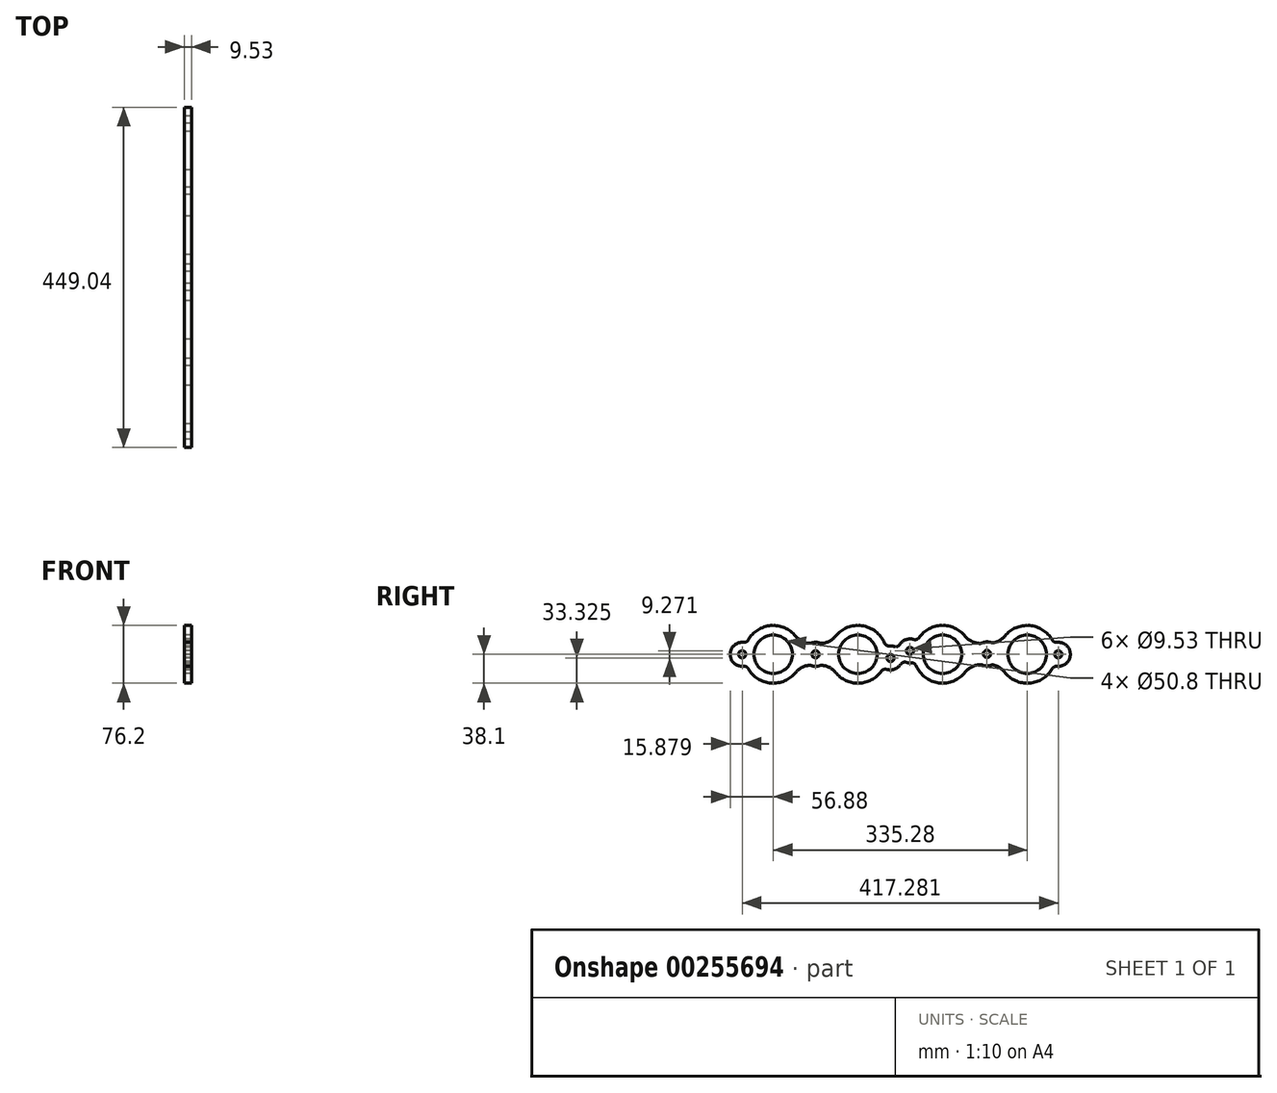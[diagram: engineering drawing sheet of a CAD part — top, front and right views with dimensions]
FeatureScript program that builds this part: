
annotation { "Feature Type Name" : "Feature", "Feature Type Description" : "" }
export const myFeature = defineFeature(function(context is Context, id is Id, definition is map)
    precondition{}
    {
        {
            var Q0;
            Q0=qCreatedBy(makeId("Right.planeOp"),FACE);
            cPlane(context, id + "F0", {"entities" : qUnion([Q0]), "cplaneType" : CPlaneType.OFFSET, "offset" : 203.2 * mm, "oppositeDirection" : true, "width" : 152.4 * mm, "height" : 152.4 * mm});
        }
        {
            var Q0;
            Q0=qCreatedBy(makeId("Top.planeOp"),FACE);
            cPlane(context, id + "F1", {"entities" : qUnion([Q0]), "cplaneType" : CPlaneType.OFFSET, "offset" : 111.76 * mm, "width" : 152.4 * mm, "height" : 152.4 * mm});
        }
        {
            var Q0;
            Q0=qCreatedBy(makeId("Front.planeOp"),FACE);
            var sketch = newSketch(context, id + "F2", { "sketchPlane" : qUnion([Q0])});
            skCircle(sketch, "E0", {"center": v(0, 0) * mm, "radius": 44.45 * mm});
            skCircle(sketch, "E1", {"center": v(0, 0) * mm, "radius": 38.1 * mm});
            skCircle(sketch, "E2", {"center": v(0, 0) * mm, "radius": 57.15 * mm});
            skSolve(sketch);
        }
        {
            var Q0;
            Q0=qCreatedBy(id+"F0.planeOp",FACE);
            var sketch = newSketch(context, id + "F3", { "sketchPlane" : qUnion([Q0])});
            skCircle(sketch, "E3", {"center": v(129.54, 111.76) * mm, "radius": 31.75 * mm});
            skCircle(sketch, "E4.1.0.0", {"center": v(241.3, 111.76) * mm, "radius": 31.75 * mm});
            skCircle(sketch, "E4.2.0.0", {"center": v(353.06, 111.76) * mm, "radius": 31.75 * mm});
            skCircle(sketch, "E4.3.0.0", {"center": v(464.82, 111.76) * mm, "radius": 31.75 * mm});
            skLineSegment(sketch, "E4.direction1", {"start": v(129.54, 111.76) * mm, "end": v(241.3, 111.76) * mm, "construction": true});
            skCircle(sketch, "E5", {"center": v(464.82, 111.76) * mm, "radius": 25.4 * mm});
            skCircle(sketch, "E6", {"center": v(353.06, 111.76) * mm, "radius": 25.4 * mm});
            skCircle(sketch, "E7", {"center": v(241.3, 111.76) * mm, "radius": 25.4 * mm});
            skCircle(sketch, "E8", {"center": v(129.54, 111.76) * mm, "radius": 25.4 * mm});
            skArc(sketch, "E9", {"start": v(497.88, 130.7) * mm, "mid": v(467.97, 149.73) * mm, "end": v(435.33, 135.88) * mm});
            skArc(sketch, "E10", {"start": v(191.04, 126.6) * mm, "mid": v(185.42, 127.64) * mm, "end": v(179.8, 126.6) * mm});
            skCircle(sketch, "E11", {"center": v(185.42, 111.76) * mm, "radius": 4.76 * mm});
            skCircle(sketch, "E12", {"center": v(88.54, 111.76) * mm, "radius": 4.76 * mm});
            skArc(sketch, "E13", {"start": v(90.27, 127.54) * mm, "mid": v(72.66, 111.76) * mm, "end": v(90.27, 95.98) * mm});
            skCircle(sketch, "E14", {"center": v(411.61, 112.33) * mm, "radius": 4.76 * mm});
            skCircle(sketch, "E15", {"center": v(505.82, 111.76) * mm, "radius": 4.76 * mm});
            skCircle(sketch, "E16", {"center": v(310.06, 116.26) * mm, "radius": 4.76 * mm});
            skCircle(sketch, "E17", {"center": v(284.3, 106.98) * mm, "radius": 4.76 * mm});
            skArc(sketch, "E18.trimOffspring", {"start": v(504.09, 95.98) * mm, "mid": v(521.7, 111.76) * mm, "end": v(504.09, 127.54) * mm});
            skPoint(sketch, "E19.visualSharp", {"position": v(94.41, 126.5) * mm});
            skArc(sketch, "E19.filletArc", {"start": v(90.27, 127.54) * mm, "mid": v(93.85, 128.2) * mm, "end": v(96.48, 130.7) * mm});
            skPoint(sketch, "E20.visualSharp", {"position": v(94.41, 97.01) * mm});
            skArc(sketch, "E20.filletArc", {"start": v(96.48, 92.82) * mm, "mid": v(93.85, 95.33) * mm, "end": v(90.27, 95.98) * mm});
            skPoint(sketch, "E21.visualSharp", {"position": v(499.95, 126.5) * mm});
            skArc(sketch, "E21.filletArc", {"start": v(497.88, 130.7) * mm, "mid": v(500.51, 128.2) * mm, "end": v(504.09, 127.54) * mm});
            skPoint(sketch, "E22.visualSharp", {"position": v(499.95, 97.01) * mm});
            skArc(sketch, "E22.filletArc", {"start": v(504.09, 95.98) * mm, "mid": v(500.51, 95.33) * mm, "end": v(497.88, 92.82) * mm});
            skArc(sketch, "E23", {"start": v(276.38, 126.63) * mm, "mid": v(246.54, 149.5) * mm, "end": v(211.6, 135.63) * mm});
            skArc(sketch, "E24", {"start": v(318.08, 96.66) * mm, "mid": v(348.18, 73.97) * mm, "end": v(383.06, 88.27) * mm});
            skArc(sketch, "E25", {"start": v(305.1, 101.18) * mm, "mid": v(308.32, 100.48) * mm, "end": v(311.62, 100.46) * mm});
            skArc(sketch, "E26", {"start": v(289.26, 122.06) * mm, "mid": v(286.08, 122.76) * mm, "end": v(282.82, 122.8) * mm});
            skArc(sketch, "E27.trimOffspring", {"start": v(314.86, 131.39) * mm, "mid": v(304.6, 131.16) * mm, "end": v(296.62, 124.71) * mm});
            skArc(sketch, "E28.trimOffspring", {"start": v(279.39, 91.9) * mm, "mid": v(289.7, 92.06) * mm, "end": v(297.74, 98.53) * mm});
            skPoint(sketch, "E29.visualSharp", {"position": v(275.05, 94.08) * mm});
            skArc(sketch, "E29.filletArc", {"start": v(279.39, 91.9) * mm, "mid": v(275.44, 91.89) * mm, "end": v(272.26, 89.55) * mm});
            skPoint(sketch, "E30.visualSharp", {"position": v(278.1, 121.6) * mm});
            skArc(sketch, "E30.filletArc", {"start": v(276.38, 126.63) * mm, "mid": v(278.97, 123.66) * mm, "end": v(282.82, 122.8) * mm});
            skPoint(sketch, "E31.visualSharp", {"position": v(294.46, 119.19) * mm});
            skArc(sketch, "E31.filletArc", {"start": v(289.26, 122.06) * mm, "mid": v(293.4, 122.12) * mm, "end": v(296.62, 124.71) * mm});
            skPoint(sketch, "E32.visualSharp", {"position": v(319.2, 129.23) * mm});
            skArc(sketch, "E32.filletArc", {"start": v(314.86, 131.39) * mm, "mid": v(318.8, 131.42) * mm, "end": v(321.96, 133.77) * mm});
            skPoint(sketch, "E33.visualSharp", {"position": v(316.32, 101.67) * mm});
            skArc(sketch, "E33.filletArc", {"start": v(318.08, 96.66) * mm, "mid": v(315.47, 99.61) * mm, "end": v(311.62, 100.46) * mm});
            skPoint(sketch, "E34.visualSharp", {"position": v(299.9, 104.05) * mm});
            skArc(sketch, "E34.filletArc", {"start": v(305.1, 101.18) * mm, "mid": v(300.96, 101.12) * mm, "end": v(297.74, 98.53) * mm});
            skArc(sketch, "E35", {"start": v(96.48, 92.82) * mm, "mid": v(126.56, 73.78) * mm, "end": v(159.24, 87.9) * mm});
            skArc(sketch, "E36.trimOffspring", {"start": v(159.24, 135.63) * mm, "mid": v(126.56, 149.74) * mm, "end": v(96.48, 130.7) * mm});
            skArc(sketch, "E37.trimOffspring", {"start": v(211.6, 87.9) * mm, "mid": v(242.34, 73.67) * mm, "end": v(272.26, 89.55) * mm});
            skPoint(sketch, "E38.visualSharp", {"position": v(164.82, 126.14) * mm});
            skArc(sketch, "E38.filletArc", {"start": v(159.24, 135.63) * mm, "mid": v(167.17, 129.08) * mm, "end": v(177.05, 126.21) * mm});
            skPoint(sketch, "E39.visualSharp", {"position": v(164.82, 97.38) * mm});
            skArc(sketch, "E39.filletArc", {"start": v(177.05, 97.3) * mm, "mid": v(167.17, 94.44) * mm, "end": v(159.24, 87.9) * mm});
            skPoint(sketch, "E40.visualSharp", {"position": v(206.02, 126.14) * mm});
            skArc(sketch, "E40.filletArc", {"start": v(193.79, 126.21) * mm, "mid": v(203.67, 129.08) * mm, "end": v(211.6, 135.63) * mm});
            skPoint(sketch, "E41.visualSharp", {"position": v(206.02, 97.38) * mm});
            skArc(sketch, "E41.filletArc", {"start": v(211.6, 87.9) * mm, "mid": v(203.67, 94.44) * mm, "end": v(193.79, 97.3) * mm});
            skArc(sketch, "E42.trimOffspring", {"start": v(434.73, 88.4) * mm, "mid": v(467.49, 73.75) * mm, "end": v(497.88, 92.82) * mm});
            skArc(sketch, "E43.trimOffspring", {"start": v(382.76, 135.63) * mm, "mid": v(351.9, 149.84) * mm, "end": v(321.96, 133.77) * mm});
            skArc(sketch, "E44.trimOffspring", {"start": v(179.8, 96.91) * mm, "mid": v(185.42, 95.89) * mm, "end": v(191.04, 96.91) * mm});
            skPoint(sketch, "E45.visualSharp", {"position": v(178.7, 126.14) * mm});
            skArc(sketch, "E45.filletArc", {"start": v(177.05, 126.21) * mm, "mid": v(178.45, 126.26) * mm, "end": v(179.8, 126.6) * mm});
            skPoint(sketch, "E46.visualSharp", {"position": v(192.15, 126.14) * mm});
            skArc(sketch, "E46.filletArc", {"start": v(191.04, 126.6) * mm, "mid": v(192.4, 126.26) * mm, "end": v(193.79, 126.21) * mm});
            skPoint(sketch, "E47.visualSharp", {"position": v(178.7, 97.38) * mm});
            skArc(sketch, "E47.filletArc", {"start": v(179.8, 96.91) * mm, "mid": v(178.45, 97.26) * mm, "end": v(177.05, 97.3) * mm});
            skPoint(sketch, "E48.visualSharp", {"position": v(192.15, 97.38) * mm});
            skArc(sketch, "E48.filletArc", {"start": v(193.79, 97.3) * mm, "mid": v(192.4, 97.26) * mm, "end": v(191.04, 96.91) * mm});
            skArc(sketch, "E49", {"start": v(405.77, 97.57) * mm, "mid": v(411.31, 96.45) * mm, "end": v(416.89, 97.35) * mm});
            skPoint(sketch, "E50.visualSharp", {"position": v(429.54, 97.38) * mm});
            skArc(sketch, "E50.filletArc", {"start": v(434.73, 88.4) * mm, "mid": v(428.37, 94.2) * mm, "end": v(420.44, 97.55) * mm});
            skPoint(sketch, "E51.visualSharp", {"position": v(429.54, 126.14) * mm});
            skArc(sketch, "E51.filletArc", {"start": v(420.3, 127) * mm, "mid": v(428.6, 130.1) * mm, "end": v(435.33, 135.88) * mm});
            skPoint(sketch, "E52.visualSharp", {"position": v(388.34, 126.14) * mm});
            skArc(sketch, "E52.filletArc", {"start": v(382.76, 135.63) * mm, "mid": v(391.4, 128.72) * mm, "end": v(402.16, 126.14) * mm});
            skPoint(sketch, "E53.visualSharp", {"position": v(388.34, 97.38) * mm});
            skArc(sketch, "E53.filletArc", {"start": v(403.56, 98) * mm, "mid": v(392.16, 95.56) * mm, "end": v(383.06, 88.27) * mm});
            skArc(sketch, "E54.trimOffspring", {"start": v(417, 127.26) * mm, "mid": v(410.9, 128.19) * mm, "end": v(404.93, 126.73) * mm});
            skPoint(sketch, "E55.visualSharp", {"position": v(403.84, 126.17) * mm});
            skArc(sketch, "E55.filletArc", {"start": v(402.16, 126.14) * mm, "mid": v(403.58, 126.28) * mm, "end": v(404.93, 126.73) * mm});
            skPoint(sketch, "E56.visualSharp", {"position": v(418.34, 126.7) * mm});
            skArc(sketch, "E56.filletArc", {"start": v(417, 127.26) * mm, "mid": v(418.63, 126.9) * mm, "end": v(420.3, 127) * mm});
            skPoint(sketch, "E57.visualSharp", {"position": v(404.88, 97.95) * mm});
            skArc(sketch, "E57.filletArc", {"start": v(405.77, 97.57) * mm, "mid": v(404.69, 97.89) * mm, "end": v(403.56, 98) * mm});
            skPoint(sketch, "E58.visualSharp", {"position": v(418.34, 97.95) * mm});
            skArc(sketch, "E58.filletArc", {"start": v(420.44, 97.55) * mm, "mid": v(418.65, 97.7) * mm, "end": v(416.89, 97.35) * mm});
            skSolve(sketch);
        }
        {
            var Q0;
            Q0=qCreatedBy(id+"F1.planeOp",FACE);
            var sketch = newSketch(context, id + "F4", { "sketchPlane" : qUnion([Q0])});
            skLineSegment(sketch, "E59.0", {"start": v(-203.2, 161.3) * mm, "end": v(-203.2, 97.8) * mm, "construction": true});
            skLineSegment(sketch, "E59.1", {"start": v(-203.2, 273.05) * mm, "end": v(-203.2, 209.55) * mm, "construction": true});
            skLineSegment(sketch, "E59.2", {"start": v(-203.2, 384.81) * mm, "end": v(-203.2, 321.31) * mm, "construction": true});
            skLineSegment(sketch, "E59.3", {"start": v(-203.2, 496.57) * mm, "end": v(-203.2, 433.07) * mm, "construction": true});
            skLineSegment(sketch, "E60", {"start": v(-203.2, 97.8) * mm, "end": v(-177.8, 97.8) * mm});
            skLineSegment(sketch, "E61.0.1.0", {"start": v(-203.2, 209.55) * mm, "end": v(-177.8, 209.55) * mm});
            skLineSegment(sketch, "E61.0.2.0", {"start": v(-203.2, 321.31) * mm, "end": v(-177.8, 321.31) * mm});
            skLineSegment(sketch, "E61.0.3.0", {"start": v(-203.2, 433.07) * mm, "end": v(-177.8, 433.07) * mm});
            skLineSegment(sketch, "E61.direction1", {"start": v(-203.2, 97.8) * mm, "end": v(-177.8, 97.8) * mm, "construction": true});
            skLineSegment(sketch, "E61.direction2", {"start": v(-203.2, 97.8) * mm, "end": v(-203.2, 209.55) * mm, "construction": true});
            skPoint(sketch, "E62", {"position": v(-190.5, 97.8) * mm});
            skPoint(sketch, "E63", {"position": v(-190.5, 209.55) * mm});
            skPoint(sketch, "E64", {"position": v(-190.5, 321.31) * mm});
            skPoint(sketch, "E65", {"position": v(-190.5, 433.07) * mm});
            skSolve(sketch);
        }
        {
            var Q0;
            Q0=qCreatedBy(makeId("Top.planeOp"),FACE);
            var sketch = newSketch(context, id + "F5", { "sketchPlane" : qUnion([Q0])});
            skLineSegment(sketch, "E66", {"start": v(-44.45, 0) * mm, "end": v(-44.45, 12.7) * mm});
            skLineSegment(sketch, "E67.0.0", {"start": v(44.45, 0) * mm, "end": v(-44.45, 0) * mm, "construction": true});
            skPoint(sketch, "E68", {"position": v(-44.45, 8.02) * mm});
            skSolve(sketch);
        }
        {
            var Q0;
            Q0=qCreatedBy(makeId("Front.planeOp"),FACE);
            cPlane(context, id + "F6", {"entities" : qUnion([Q0]), "cplaneType" : CPlaneType.OFFSET, "offset" : 76.2 * mm, "oppositeDirection" : true, "width" : 152.4 * mm, "height" : 152.4 * mm});
        }
        {
            var Q0;
            Q0=sQuery(id+"F4.wireOp",VERTEX,"E61.direction2.start");
            var Q1;
            Q1=sQuery(id+"F4.wireOp",VERTEX,"E60.end");
            var Q2;
            Q2=sQuery(id+"F5.wireOp",VERTEX,"E66.end");
            cPlane(context, id + "F7", {"entities" : qUnion([Q0, Q1, Q2]), "cplaneType" : CPlaneType.THREE_POINT, "offset" : 25.4 * mm, "width" : 152.4 * mm, "height" : 152.4 * mm});
        }
        {
            var Q0;
            Q0=makeQuery(id+"F3.imprint","IMPRINT",FACE,{"disambiguationData":[TD([[makeQuery(id+"F3.imprint","IMPRINT",EDGE,{"derivedFrom":sQuery(id+"F3.wireOp",EDGE,"E3")}),-1.0]])]});
            var Q1;
            Q1=makeQuery(id+"F3.imprint","IMPRINT",FACE,{"disambiguationData":[TD([[makeQuery(id+"F3.imprint","IMPRINT",EDGE,{"derivedFrom":sQuery(id+"F3.wireOp",EDGE,"E3")}),1.0]])]});
            var Q2;
            Q2=makeQuery(id+"F3.imprint","IMPRINT",FACE,{"disambiguationData":[TD([[makeQuery(id+"F3.imprint","IMPRINT",EDGE,{"derivedFrom":sQuery(id+"F3.wireOp",EDGE,"E4.1.0.0")}),1.0]])]});
            var Q3;
            Q3=makeQuery(id+"F3.imprint","IMPRINT",FACE,{"disambiguationData":[TD([[makeQuery(id+"F3.imprint","IMPRINT",EDGE,{"derivedFrom":sQuery(id+"F3.wireOp",EDGE,"E4.2.0.0")}),1.0]])]});
            var Q4;
            Q4=makeQuery(id+"F3.imprint","IMPRINT",FACE,{"disambiguationData":[TD([[makeQuery(id+"F3.imprint","IMPRINT",EDGE,{"derivedFrom":sQuery(id+"F3.wireOp",EDGE,"E4.3.0.0")}),1.0]])]});
            extrude(context, id + "F8", {"entities" : qUnion([Q0, Q1, Q2, Q3, Q4]), "depth" : 9.52 * mm});
        }
    });
